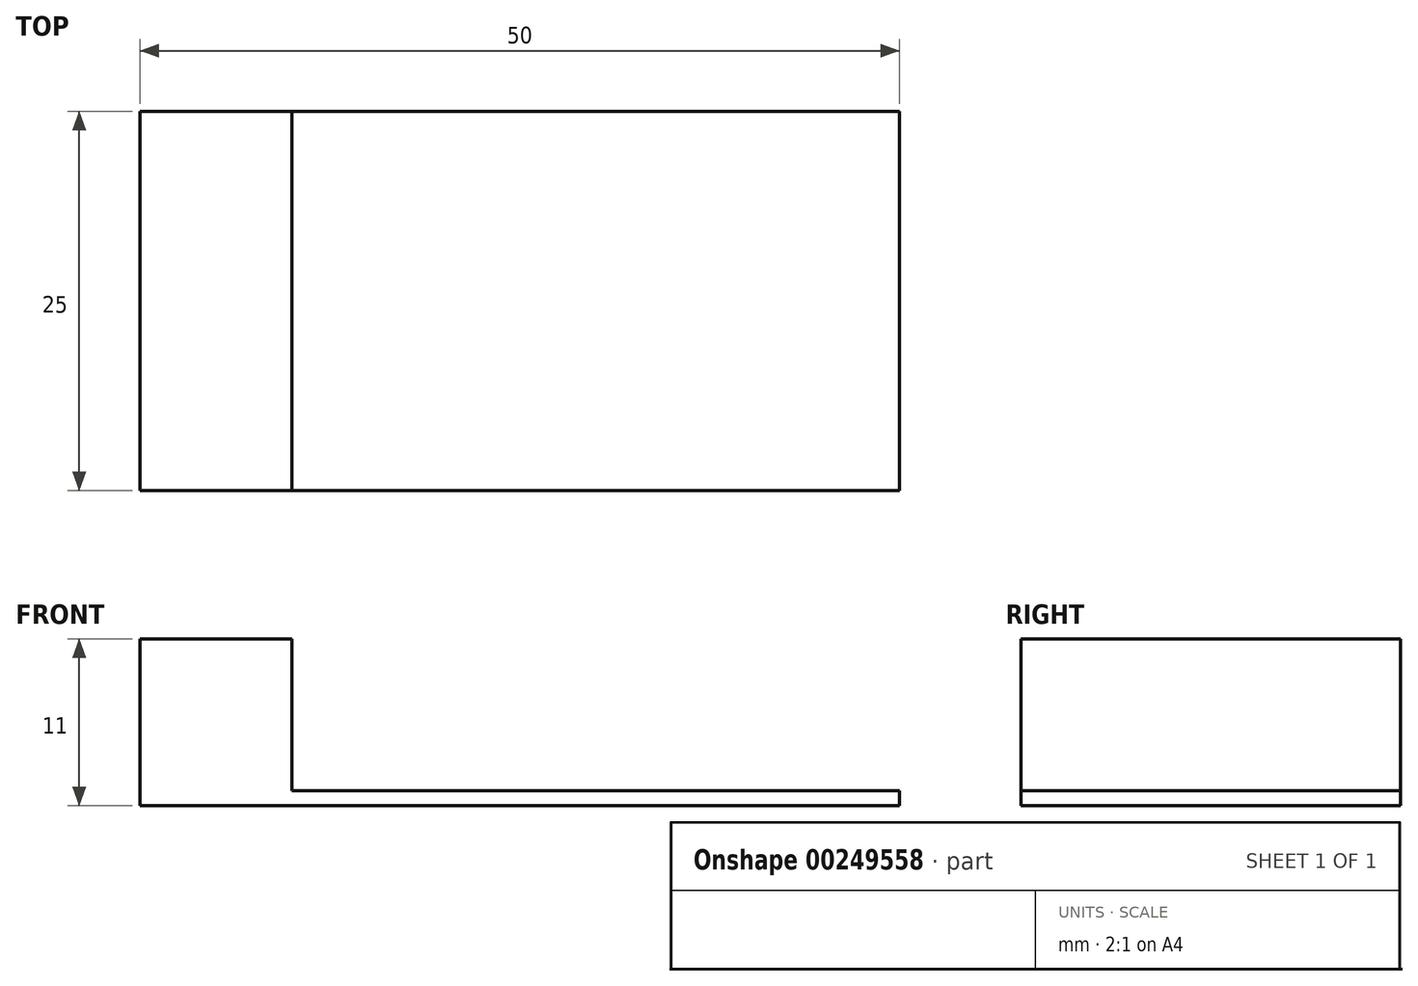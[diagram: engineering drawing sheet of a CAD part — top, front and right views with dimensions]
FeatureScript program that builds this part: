
annotation { "Feature Type Name" : "Feature", "Feature Type Description" : "" }
export const myFeature = defineFeature(function(context is Context, id is Id, definition is map)
    precondition{}
    {
        {
            var Q0;
            Q0=qCreatedBy(makeId("Top.planeOp"),FACE);
            var sketch = newSketch(context, id + "F0", { "sketchPlane" : qUnion([Q0])});
            skLineSegment(sketch, "E0", {"start": v(0, 0) * mm, "end": v(50, 0) * mm});
            skLineSegment(sketch, "E1", {"start": v(0, 0) * mm, "end": v(0, 25) * mm});
            skLineSegment(sketch, "E2", {"start": v(0, 25) * mm, "end": v(50, 25) * mm});
            skLineSegment(sketch, "E3", {"start": v(50, 0) * mm, "end": v(50, 25) * mm});
            skSolve(sketch);
        }
        {
            var Q0;
            Q0 = qSketchRegion(id + "F0", true);
            extrude(context, id + "F1", {"entities" : qUnion([Q0]), "oppositeDirection" : true, "depth" : 1 * mm});
        }
        {
            var Q0;
            Q0=makeQuery(id+"F1.opExtrude","CAP_FACE",FACE,{"disambiguationData":[OSD([sQuery(id+"F0.wireOp",EDGE,"E0"),sQuery(id+"F0.wireOp",EDGE,"E1"),sQuery(id+"F0.wireOp",EDGE,"E2"),sQuery(id+"F0.wireOp",EDGE,"E3")])],"isStart":true});
            var sketch = newSketch(context, id + "F2", { "sketchPlane" : qUnion([Q0])});
            skLineSegment(sketch, "E4", {"start": v(0, 0) * mm, "end": v(10, 0) * mm});
            skLineSegment(sketch, "E5", {"start": v(10, 0) * mm, "end": v(10, 25) * mm});
            skLineSegment(sketch, "E6", {"start": v(10, 25) * mm, "end": v(0, 25) * mm});
            skLineSegment(sketch, "E7", {"start": v(0, 25) * mm, "end": v(0, 0) * mm});
            skSolve(sketch);
        }
        {
            var Q0;
            Q0 = qSketchRegion(id + "F2", true);
            extrude(context, id + "F3", {"entities" : qUnion([Q0]), "operationType" : NewBodyOperationType.ADD, "depth" : 10 * mm});
        }
    });
